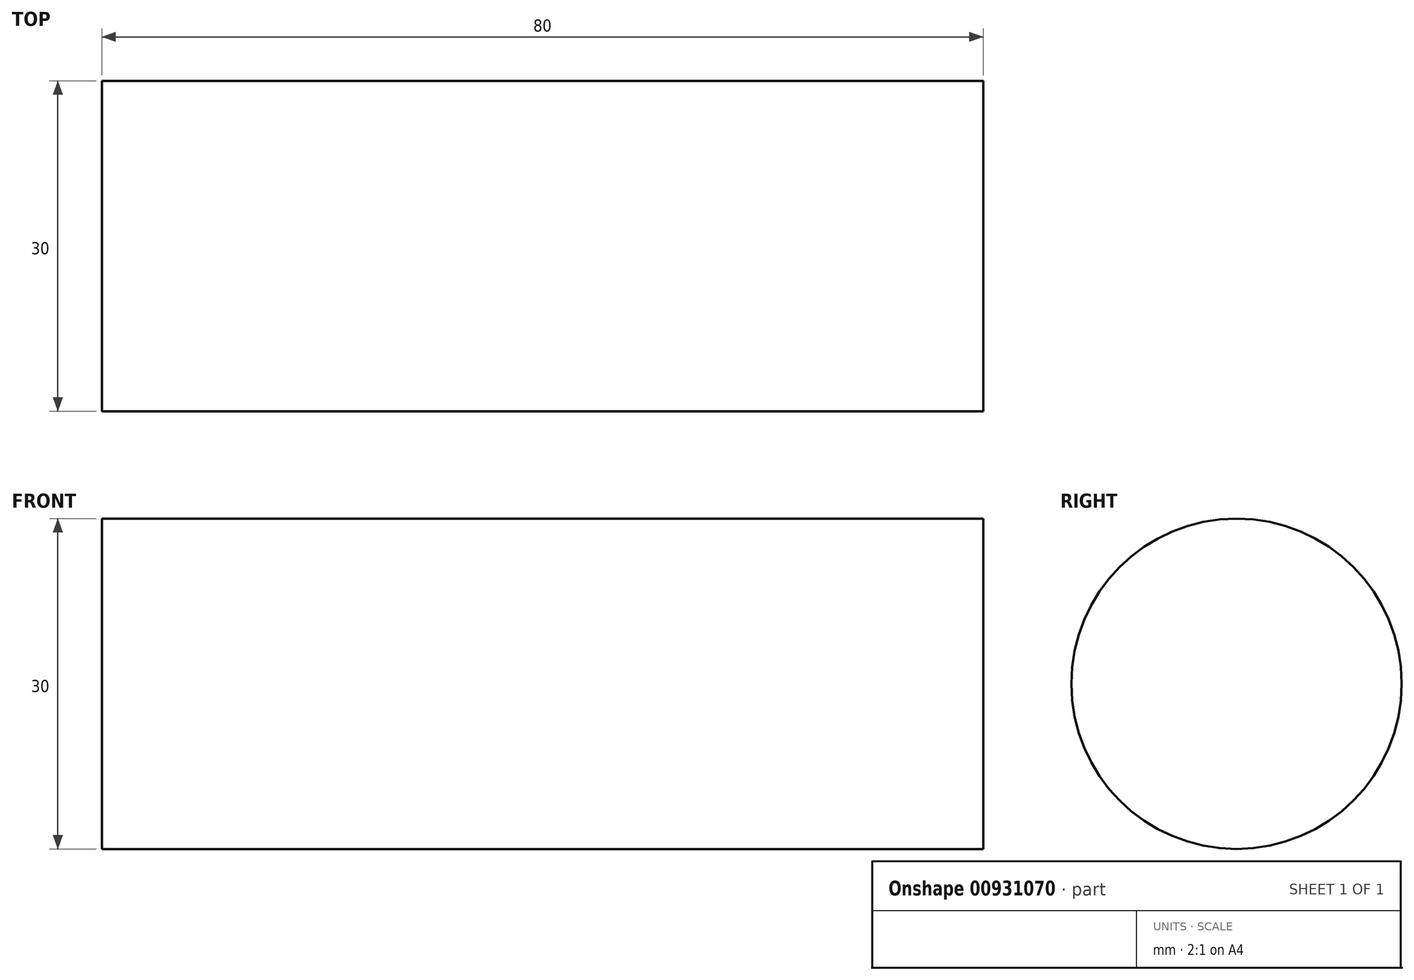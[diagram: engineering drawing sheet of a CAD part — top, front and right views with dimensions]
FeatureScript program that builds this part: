
annotation { "Feature Type Name" : "Feature", "Feature Type Description" : "" }
export const myFeature = defineFeature(function(context is Context, id is Id, definition is map)
    precondition{}
    {
        {
            var Q0;
            Q0=qCreatedBy(makeId("Right.planeOp"),FACE);
            var sketch = newSketch(context, id + "F0", { "sketchPlane" : qUnion([Q0])});
            skCircle(sketch, "E0", {"center": v(0, 0) * mm, "radius": 15 * mm});
            skSolve(sketch);
        }
        {
            var Q0;
            Q0=makeQuery(id+"F0.imprint","IMPRINT",FACE,{"disambiguationData":[TD([[makeQuery(id+"F0.imprint","IMPRINT",EDGE,{"derivedFrom":sQuery(id+"F0.wireOp",EDGE,"E0")}),1.0]])]});
            extrude(context, id + "F1", {"entities" : qUnion([Q0]), "depth" : 80 * mm, "offsetDistance" : 25 * mm, "symmetric" : true});
        }
    });
